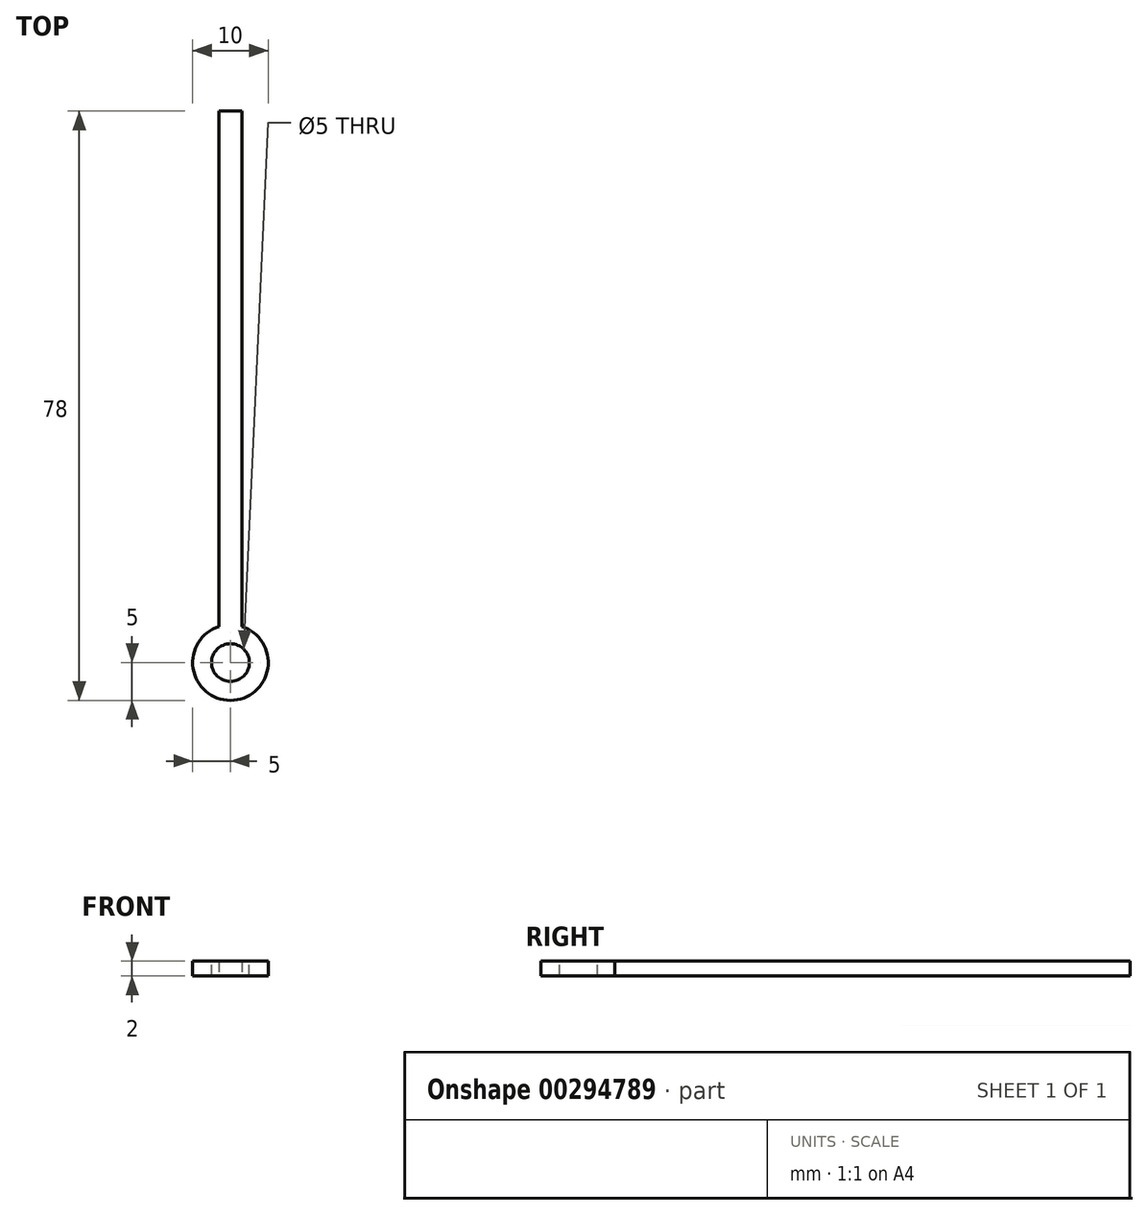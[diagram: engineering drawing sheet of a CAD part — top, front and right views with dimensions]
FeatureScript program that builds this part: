
annotation { "Feature Type Name" : "Feature", "Feature Type Description" : "" }
export const myFeature = defineFeature(function(context is Context, id is Id, definition is map)
    precondition{}
    {
        {
            var Q0;
            Q0=qCreatedBy(makeId("Top.planeOp"),FACE);
            var sketch = newSketch(context, id + "F0", { "sketchPlane" : qUnion([Q0])});
            skCircle(sketch, "E0", {"center": v(0, 0) * mm, "radius": 5 * mm});
            skLineSegment(sketch, "E1", {"start": v(-1.5, 73) * mm, "end": v(1.5, 73) * mm});
            skLineSegment(sketch, "E2", {"start": v(1.5, 73) * mm, "end": v(1.5, 0) * mm});
            skLineSegment(sketch, "E3", {"start": v(-1.5, 73) * mm, "end": v(-1.5, 0) * mm});
            skLineSegment(sketch, "E4", {"start": v(-1.5, 0) * mm, "end": v(1.5, 0) * mm});
            skSolve(sketch);
        }
        {
            var Q0;
            {var subQ5=sQuery(id+"F0.wireOp",EDGE,"E4");Q0=makeQuery(id+"F0.imprint","IMPRINT",FACE,{"disambiguationData":[TD([[makeQuery(id+"F0.imprint","IMPRINT",EDGE,{"derivedFrom":subQ5}),-1.0]])]});}
            var Q1;
            {var subQ5=sQuery(id+"F0.wireOp",EDGE,"E4");Q1=makeQuery(id+"F0.imprint","IMPRINT",FACE,{"disambiguationData":[TD([[makeQuery(id+"F0.imprint","IMPRINT",EDGE,{"derivedFrom":subQ5}),1.0]])]});}
            var Q2;
            {var subQ5=sQuery(id+"F0.wireOp",EDGE,"E1");Q2=makeQuery(id+"F0.imprint","IMPRINT",FACE,{"disambiguationData":[TD([[makeQuery(id+"F0.imprint","IMPRINT",EDGE,{"derivedFrom":subQ5}),-1.0]])]});}
            extrude(context, id + "F1", {"entities" : qUnion([Q0, Q1, Q2]), "depth" : 2 * mm});
        }
        {
            var Q0;
            Q0=makeQuery(id+"F1.opExtrude","CAP_FACE",FACE,{"disambiguationData":[OSD([sQuery(id+"F0.wireOp",EDGE,"E0"),sQuery(id+"F0.wireOp",EDGE,"E1"),sQuery(id+"F0.wireOp",EDGE,"E2"),sQuery(id+"F0.wireOp",EDGE,"E3")])],"isStart":false});
            var sketch = newSketch(context, id + "F2", { "sketchPlane" : qUnion([Q0])});
            skCircle(sketch, "E5", {"center": v(0, 0) * mm, "radius": 2.5 * mm});
            skSolve(sketch);
        }
        {
            var Q0;
            Q0 = qSketchRegion(id + "F2", true);
            extrude(context, id + "F3", {"entities" : qUnion([Q0]), "operationType" : NewBodyOperationType.REMOVE, "endBound" : BoundingType.THROUGH_ALL, "oppositeDirection" : true, "depth" : 25 * mm});
        }
    });
